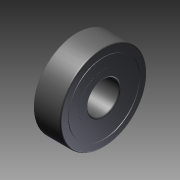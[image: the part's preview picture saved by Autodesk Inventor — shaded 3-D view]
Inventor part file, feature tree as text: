
AUTODESK INVENTOR PART (.ipt)
format: ipt  version: 2016 (Build 200138000, 138)  size: 169,472 bytes
history: native  units: mm
features: other x7, revolve x3, sketch x3
ambient origin geometry x8: Origin, YZ Plane, XZ Plane, XY Plane, X Axis, Y Axis, Z Axis, Center Point
bodies: Solid1 (feature_tree)
feature tree (13):
  revolve  "Revolution1"  Angle=360.0deg
  revolve  "Revolution2"  [1 undecoded]
  revolve  "Revolution3"  [1 undecoded]
  other  "ff_2_XY"
  other  "ff_2_YZ"
  other  "ff_2_ZX"
  other  "ff_2_X"
  other  "ff_2_Y"
  other  "ff_2_Z"
  other  "ff_2_Center"
  sketch  "Sketch_1"  dims[d0=360.0deg d1=360.0deg]
  sketch  "Sketch_2"  dims[d2=360.0deg]
  sketch  "Sketch_3"
note: 2 required parameter values undecoded (feature->parameter linkage not recoverable at this tier; creation-order binding heuristic only, values carry confidence <= 0.55)
